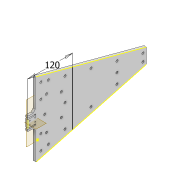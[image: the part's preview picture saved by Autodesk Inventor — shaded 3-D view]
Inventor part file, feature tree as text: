
AUTODESK INVENTOR PART (.ipt)
format: ipt  version: 2022 (Build 260153000, 153)  size: 271,872 bytes
history: native  units: mm
features: sketch x6, extrude x5, plane x2, thicken_offset x2, fillet x2, projected_geometry x2, mirror x1, chamfer x1
ambient origin geometry x8: Origin, YZ Plane, XZ Plane, XY Plane, X Axis, Y Axis, Z Axis, Center Point
bodies: Solid1 (feature_tree)
feature tree (21):
  extrude  "Extrusion1"  Depth=100.0mm
  extrude  "Extrusion2"  Depth=5.0mm
  plane  "Work Plane1"
  extrude  "Extrusion11"  Depth=10.0mm
  plane  "Work Plane3"
  thicken_offset  "Thicken1"
  thicken_offset  "Thicken2"
  extrude  "Extrusion12"  Depth=5.0mm
  extrude  "Extrusion13"  Depth=3.1mm
  mirror  "Mirror1"
  chamfer  "Chamfer1"  Distance=20.0mm
  fillet  "Fillet2"  Radius=3.0mm
  fillet  "Fillet3"  Radius=3.0mm
  sketch  "Sketch18"  dims[d13=5.0mm d14=20.0mm d15=0.0mm d57=3.0mm d58=3.0mm d59=3.0mm d60=3.0mm d61=5.0mm d62=5.0mm d63=5.0mm d64=5.0mm d65=5.0mm d67=5.0mm d69=5.0mm d70=5.0mm d71=180.0mm d72=0.0mm d74=1.0mm d75=0.5mm d76=1.0mm d77=0.5mm d78=50.0mm d79=50.0mm d80=300.0mm d81=80.0mm d82=80.0mm d83=6.0mm d84=0.0mm d85=5.95mm d86=15.0mm d87=20.0mm d88=5.95mm d89=150.0mm d90=55.0mm d91=5.95mm d92=290.0mm d93=90.0mm d94=100.0mm d95=0.0mm d96=5.95mm d97=80.0mm d98=5.95mm d99=220.0mm d100=6.0mm d101=2.0mm d102=45.0deg d103=2.0mm d104=5.95mm d105=80.0mm d106=38.0mm d107=5.95mm d108=220.0mm d109=73.0mm d110=5.95mm d111=15.0mm d112=40.0mm d113=0.8mm d114=120.0mm d115=5.95mm d116=30.0mm d117=70.0mm d118=5.95mm d119=35.0mm d120=75.0mm d121=5.95mm d122=30.0mm d123=45.0mm d124=5.95mm d125=25.0mm]
  sketch  "Sketch1"  dims[d0=6.0mm d1=100.0mm]
  sketch  "Sketch3"  dims[d2=5.0mm d3=0.0mm d6=50.0mm]
  projected_geometry  "Projected Loop2"
  sketch  "Sketch13"  dims[d7=100.0mm d8=10.0mm]
  sketch  "Sketch14"  dims[d9=10.0mm d10=5.0mm]
  projected_geometry  "Projected Loop15"
  sketch  "Sketch15"  dims[d11=3.1mm d12=3.1mm]
